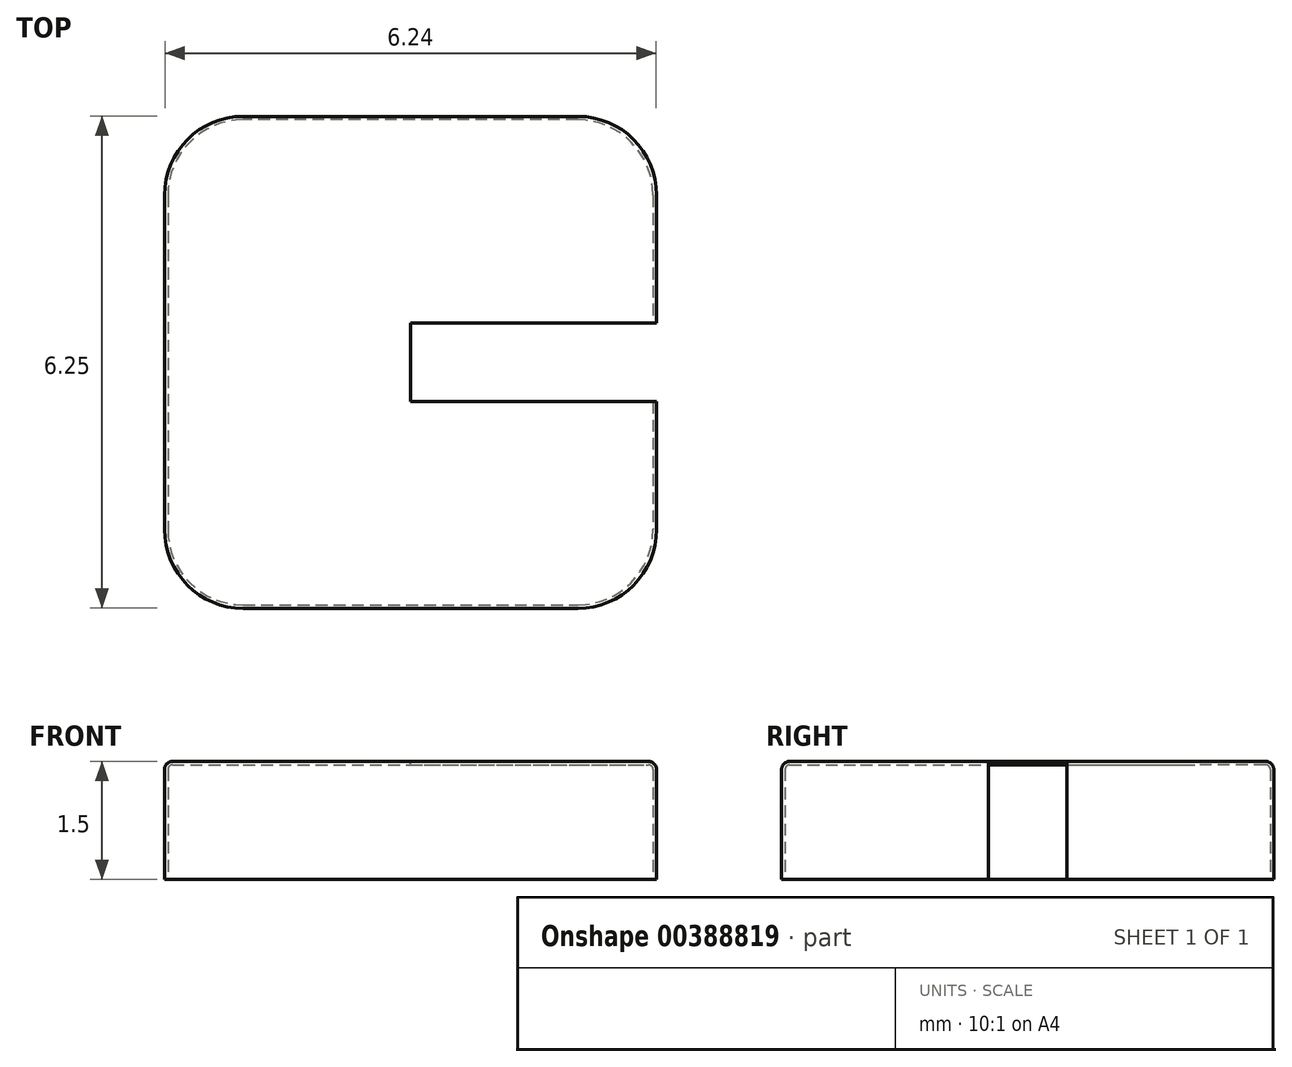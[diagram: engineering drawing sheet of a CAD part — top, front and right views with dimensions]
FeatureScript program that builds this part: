
annotation { "Feature Type Name" : "Feature", "Feature Type Description" : "" }
export const myFeature = defineFeature(function(context is Context, id is Id, definition is map)
    precondition{}
    {
        {
            assignVariable(context, id + "F0", {"name" : "round", "anyValue" : 0.1});
        }
        {
            assignVariable(context, id + "F1", {"name" : "height", "anyValue" : 1.5});
        }
        {
            assignVariable(context, id + "F2", {"name" : "thickness", "anyValue" : 0.04});
        }
        {
            var Q0;
            Q0=qCreatedBy(makeId("Top.planeOp"),FACE);
            var sketch = newSketch(context, id + "F3", { "sketchPlane" : qUnion([Q0])});
            skLineSegment(sketch, "E0.bottom", {"start": v(0, 0) * mm, "end": v(3.12, 0) * mm});
            skLineSegment(sketch, "E0.top", {"start": v(0, -3.12) * mm, "end": v(2.12, -3.12) * mm});
            skLineSegment(sketch, "E0.left", {"start": v(0, 0) * mm, "end": v(0, -3.12) * mm});
            skLineSegment(sketch, "E0.right", {"start": v(3.12, 0) * mm, "end": v(3.12, -2.12) * mm});
            skPoint(sketch, "E1.visualSharp", {"position": v(3.12, -3.12) * mm});
            skArc(sketch, "E1.filletArc", {"start": v(2.12, -3.12) * mm, "mid": v(2.83, -2.83) * mm, "end": v(3.12, -2.12) * mm});
            skSolve(sketch);
        }
        {
            var Q0;
            Q0 = qSketchRegion(id + "F3", true);
            extrude(context, id + "F4", {"entities" : qUnion([Q0]), "depth" : (getVariable(context, 'height')) * mm});
        }
        {
            var Q0;
            Q0=makeQuery(id+"F4.opExtrude","CAP_EDGE",EDGE,{"disambiguationData":[OSD([sQuery(id+"F3.wireOp",EDGE,"E0.top")])],"isStart":false});
            var Q1;
            Q1=makeQuery(id+"F4.opExtrude","CAP_EDGE",EDGE,{"disambiguationData":[OSD([sQuery(id+"F3.wireOp",EDGE,"E1.filletArc")])],"isStart":false});
            var Q2;
            Q2=makeQuery(id+"F4.opExtrude","CAP_EDGE",EDGE,{"disambiguationData":[OSD([sQuery(id+"F3.wireOp",EDGE,"E0.right")])],"isStart":false});
            fillet(context, id + "F5", {"entities" : qUnion([Q0, Q1, Q2]), "radius" : (getVariable(context, 'round')) * mm, "tangentPropagation" : true, "allowEdgeOverflow" : false});
        }
        {
            var Q0;
            Q0=makeQuery(id+"F4.opExtrude","SWEPT_BODY",BODY,{"disambiguationData":[OSD([sQuery(id+"F3.wireOp",EDGE,"E0.bottom"),sQuery(id+"F3.wireOp",EDGE,"E0.top"),sQuery(id+"F3.wireOp",EDGE,"E0.left"),sQuery(id+"F3.wireOp",EDGE,"E0.right"),sQuery(id+"F3.wireOp",EDGE,"E1.filletArc")])]});
            var Q1;
            Q1=makeQuery(id+"F4.opExtrude","SWEPT_EDGE",EDGE,{"disambiguationData":[OSD([sQuery(id+"F3.wireOp",EDGE,"E0.bottom"),sQuery(id+"F3.wireOp",EDGE,"E0.left")])]});
            circularPattern(context, id + "F6", {"operationType" : NewBodyOperationType.ADD, "entities" : qUnion([Q0]), "axis" : qUnion([Q1]), "angle" : 360 * degree, "instanceCount" : 4, "equalSpace" : true});
        }
        {
            var Q0;
            {var subQ0=makeQuery(id+"F4.opExtrude","CAP_FACE",FACE,{"disambiguationData":[OSD([sQuery(id+"F3.wireOp",EDGE,"E0.bottom"),sQuery(id+"F3.wireOp",EDGE,"E0.top"),sQuery(id+"F3.wireOp",EDGE,"E0.left"),sQuery(id+"F3.wireOp",EDGE,"E0.right"),sQuery(id+"F3.wireOp",EDGE,"E1.filletArc")])],"isStart":true});Q0=makeQuery(id+"F6.boolean.opBoolean","MERGE",FACE,{"derivedFrom":[subQ0,makeQuery(id+"F6.opPattern","COPY",FACE,{"derivedFrom":subQ0,"instanceName":"1"}),makeQuery(id+"F6.opPattern","COPY",FACE,{"derivedFrom":subQ0,"instanceName":"2"}),makeQuery(id+"F6.opPattern","COPY",FACE,{"derivedFrom":subQ0,"instanceName":"3"})]});}
            var Q1;
            Q1=makeQuery(id+"F4.opExtrude","SWEPT_BODY",BODY,{"disambiguationData":[OSD([sQuery(id+"F3.wireOp",EDGE,"E0.bottom"),sQuery(id+"F3.wireOp",EDGE,"E0.top"),sQuery(id+"F3.wireOp",EDGE,"E0.left"),sQuery(id+"F3.wireOp",EDGE,"E0.right"),sQuery(id+"F3.wireOp",EDGE,"E1.filletArc")])]});
            shell(context, id + "F7", {"entities" : qUnion([Q0]), "parts" : qUnion([Q1]), "thickness" : (getVariable(context, 'thickness')) * mm});
        }
        {
            var Q0;
            Q0=qCreatedBy(makeId("Front.planeOp"),FACE);
            var sketch = newSketch(context, id + "F8", { "sketchPlane" : qUnion([Q0])});
            skPoint(sketch, "E2.middle", {"position": v(0, 0) * mm});
            skLineSegment(sketch, "E3.bottom", {"start": v(0, 0) * mm, "end": v(6.25, 0) * mm});
            skLineSegment(sketch, "E3.top", {"start": v(0, 12.56) * mm, "end": v(6.25, 12.56) * mm});
            skLineSegment(sketch, "E3.left", {"start": v(0, 0) * mm, "end": v(0, 12.56) * mm});
            skLineSegment(sketch, "E3.right", {"start": v(6.25, 0) * mm, "end": v(6.25, 12.56) * mm});
            skSolve(sketch);
        }
        {
            var Q0;
            Q0 = qSketchRegion(id + "F8", true);
            extrude(context, id + "F9", {"entities" : qUnion([Q0]), "operationType" : NewBodyOperationType.REMOVE, "endBound" : BoundingType.SYMMETRIC, "oppositeDirection" : true, "depth" : 1 * mm});
        }
    });
